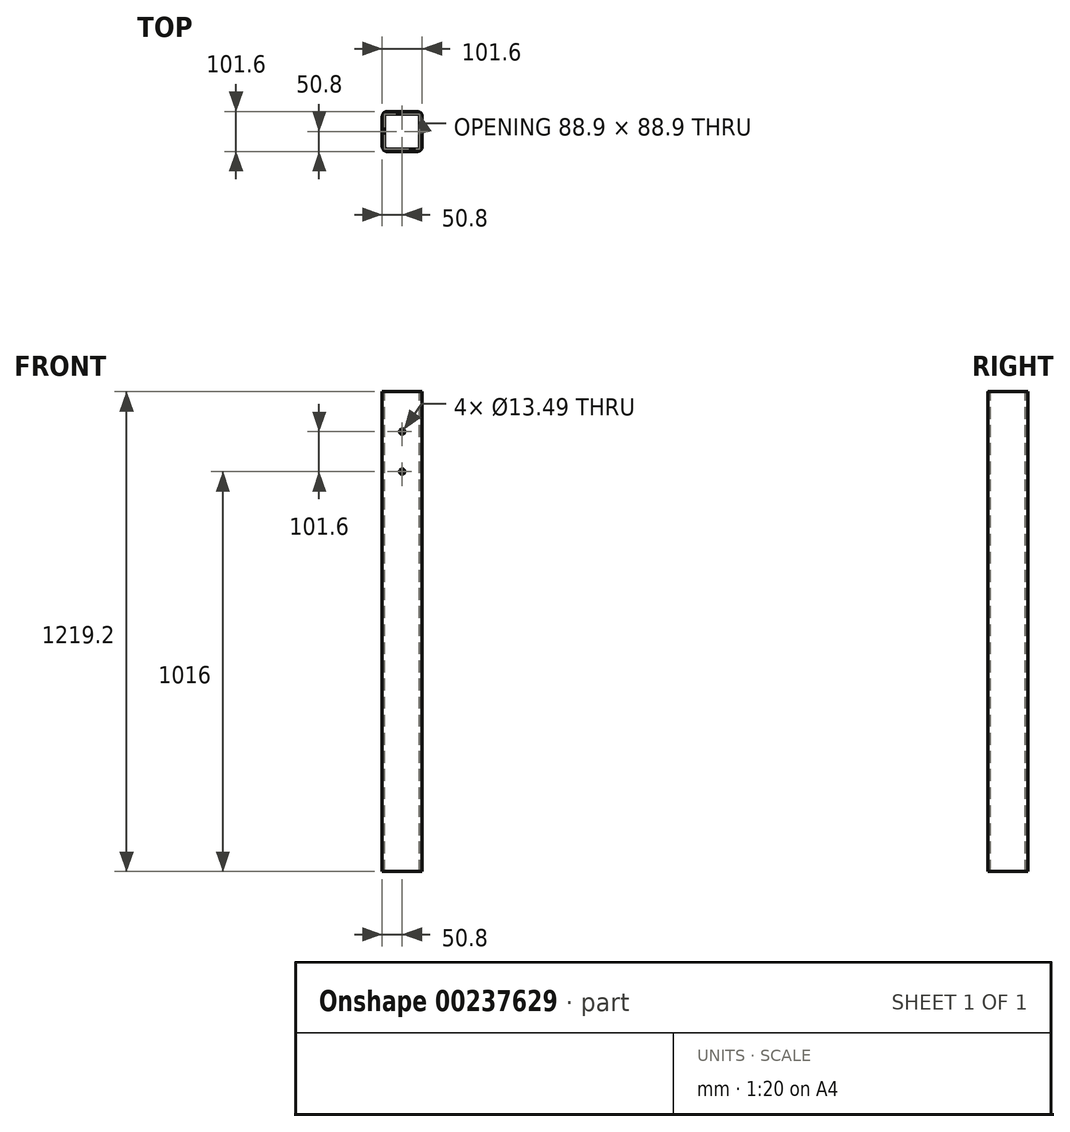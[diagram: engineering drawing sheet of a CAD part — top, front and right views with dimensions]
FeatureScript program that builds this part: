
annotation { "Feature Type Name" : "Feature", "Feature Type Description" : "" }
export const myFeature = defineFeature(function(context is Context, id is Id, definition is map)
    precondition{}
    {
        {
            var Q0;
            Q0=qCreatedBy(makeId("Top.planeOp"),FACE);
            var sketch = newSketch(context, id + "F0", { "sketchPlane" : qUnion([Q0])});
            skLineSegment(sketch, "E0.bottom", {"start": v(-50.8, 50.8) * mm, "end": v(50.8, 50.8) * mm});
            skLineSegment(sketch, "E0.top", {"start": v(-50.8, -50.8) * mm, "end": v(50.8, -50.8) * mm});
            skLineSegment(sketch, "E0.left", {"start": v(-50.8, 50.8) * mm, "end": v(-50.8, -50.8) * mm});
            skLineSegment(sketch, "E0.right", {"start": v(50.8, 50.8) * mm, "end": v(50.8, -50.8) * mm});
            skPoint(sketch, "E0.middle", {"position": v(0, 0) * mm});
            skSolve(sketch);
        }
        {
            var Q0;
            Q0 = qSketchRegion(id + "F0", true);
            extrude(context, id + "F1", {"entities" : qUnion([Q0]), "endBound" : BoundingType.SYMMETRIC, "depth" : 1219.2 * mm});
        }
        {
            var Q0;
            Q0=makeQuery(id+"F1.opExtrude","SWEPT_EDGE",EDGE,{"disambiguationData":[OSD([sQuery(id+"F0.wireOp",EDGE,"E0.bottom"),sQuery(id+"F0.wireOp",EDGE,"E0.left")])]});
            var Q1;
            Q1=makeQuery(id+"F1.opExtrude","SWEPT_EDGE",EDGE,{"disambiguationData":[OSD([sQuery(id+"F0.wireOp",EDGE,"E0.bottom"),sQuery(id+"F0.wireOp",EDGE,"E0.right")])]});
            var Q2;
            Q2=makeQuery(id+"F1.opExtrude","SWEPT_EDGE",EDGE,{"disambiguationData":[OSD([sQuery(id+"F0.wireOp",EDGE,"E0.top"),sQuery(id+"F0.wireOp",EDGE,"E0.right")])]});
            var Q3;
            Q3=makeQuery(id+"F1.opExtrude","SWEPT_EDGE",EDGE,{"disambiguationData":[OSD([sQuery(id+"F0.wireOp",EDGE,"E0.top"),sQuery(id+"F0.wireOp",EDGE,"E0.left")])]});
            fillet(context, id + "F2", {"entities" : qUnion([Q0, Q1, Q2, Q3]), "radius" : 12.7 * mm, "tangentPropagation" : true, "allowEdgeOverflow" : false});
        }
        {
            var Q0;
            Q0=qCreatedBy(makeId("Top.planeOp"),FACE);
            var sketch = newSketch(context, id + "F3", { "sketchPlane" : qUnion([Q0])});
            skLineSegment(sketch, "E1.0", {"start": v(-38.1, 44.45) * mm, "end": v(38.1, 44.45) * mm});
            skLineSegment(sketch, "E1.1", {"start": v(-44.45, 38.1) * mm, "end": v(-44.45, -38.1) * mm});
            skLineSegment(sketch, "E1.2", {"start": v(-38.1, -44.45) * mm, "end": v(38.1, -44.45) * mm});
            skLineSegment(sketch, "E1.3", {"start": v(44.45, 38.1) * mm, "end": v(44.45, -38.1) * mm});
            skPoint(sketch, "E2.visualSharp", {"position": v(-44.45, 44.45) * mm});
            skArc(sketch, "E2.filletArc", {"start": v(-38.1, 44.45) * mm, "mid": v(-42.6, 42.6) * mm, "end": v(-44.45, 38.1) * mm});
            skPoint(sketch, "E3.visualSharp", {"position": v(-44.45, -44.45) * mm});
            skArc(sketch, "E3.filletArc", {"start": v(-44.45, -38.1) * mm, "mid": v(-42.6, -42.6) * mm, "end": v(-38.1, -44.45) * mm});
            skPoint(sketch, "E4.visualSharp", {"position": v(44.45, -44.45) * mm});
            skArc(sketch, "E4.filletArc", {"start": v(38.1, -44.45) * mm, "mid": v(42.6, -42.6) * mm, "end": v(44.45, -38.1) * mm});
            skPoint(sketch, "E5.visualSharp", {"position": v(44.45, 44.45) * mm});
            skArc(sketch, "E5.filletArc", {"start": v(44.45, 38.1) * mm, "mid": v(42.6, 42.6) * mm, "end": v(38.1, 44.45) * mm});
            skSolve(sketch);
        }
        {
            var Q0;
            Q0 = qSketchRegion(id + "F3", true);
            extrude(context, id + "F4", {"entities" : qUnion([Q0]), "operationType" : NewBodyOperationType.REMOVE, "endBound" : BoundingType.THROUGH_ALL, "oppositeDirection" : true, "depth" : 25.4 * mm, "hasSecondDirection" : true, "secondDirectionBound" : SecondDirectionBoundingType.THROUGH_ALL, "secondDirectionOppositeDirection" : false, "secondDirectionDepth" : 25.4 * mm});
        }
        {
            var Q0;
            Q0=makeQuery(id+"F1.opExtrude","SWEPT_FACE",FACE,{"disambiguationData":[OSD([sQuery(id+"F0.wireOp",EDGE,"E0.top")])]});
            var sketch = newSketch(context, id + "F5", { "sketchPlane" : qUnion([Q0])});
            skLineSegment(sketch, "E6", {"start": v(0, 609.6) * mm, "end": v(0, 508) * mm, "construction": true});
            skPoint(sketch, "E6.endSnap0", {"position": v(0, 609.6) * mm});
            skLineSegment(sketch, "E7", {"start": v(0, 508) * mm, "end": v(0, 406.4) * mm, "construction": true});
            skLineSegment(sketch, "E8", {"start": v(0, 406.4) * mm, "end": v(0, 304.8) * mm, "construction": true});
            skSolve(sketch);
        }
        {
            var Q0;
            Q0=sQuery(id+"F5.wireOp",VERTEX,"E7.start");
            var Q1;
            Q1=sQuery(id+"F5.wireOp",VERTEX,"E8.start");
            var Q2;
            Q2=makeQuery(id+"F1.opExtrude","SWEPT_BODY",BODY,{"disambiguationData":[OSD([sQuery(id+"F0.wireOp",EDGE,"E0.bottom"),sQuery(id+"F0.wireOp",EDGE,"E0.top"),sQuery(id+"F0.wireOp",EDGE,"E0.left"),sQuery(id+"F0.wireOp",EDGE,"E0.right")])]});
            hole(context, id + "F6", {"style" : HoleStyle.SIMPLE, "endStyle" : HoleEndStyle.THROUGH, "standardTappedOrClearance" : lookupTablePath({ "standard" : "ANSI", "fit" : "Normal (ASME)", "size" : "1/2", "type" : "Clearance" }), "standardBlindInLast" : lookupTablePath({ "fit" : "Free", "standard" : "ANSI", "size" : "1/2", "type" : "Clearance" }), "holeDiameter" : 13.5 * mm, "locations" : qUnion([Q0, Q1]), "scope" : qUnion([Q2]), "isTappedThrough" : true});
        }
    });
